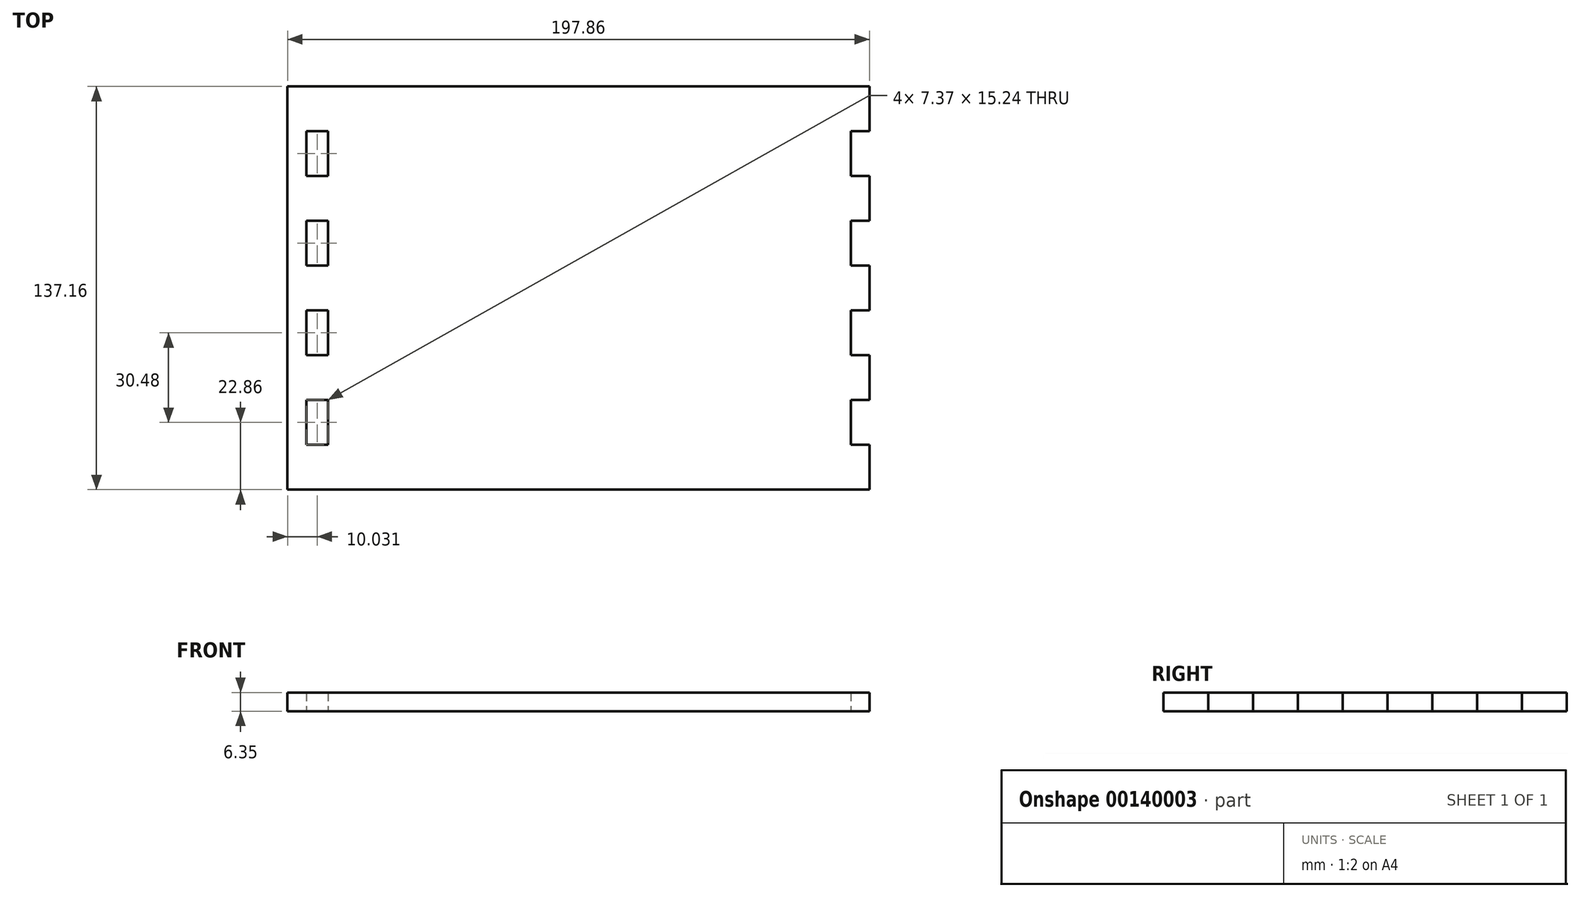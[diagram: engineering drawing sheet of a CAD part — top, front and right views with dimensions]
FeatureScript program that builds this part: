
annotation { "Feature Type Name" : "Feature", "Feature Type Description" : "" }
export const myFeature = defineFeature(function(context is Context, id is Id, definition is map)
    precondition{}
    {
        {
            var Q0;
            Q0=qCreatedBy(makeId("Top.planeOp"),FACE);
            var sketch = newSketch(context, id + "F0", { "sketchPlane" : qUnion([Q0])});
            skLineSegment(sketch, "E0.bottom", {"start": v(-69.3, 76.2) * mm, "end": v(108.5, 76.2) * mm});
            skLineSegment(sketch, "E0.top", {"start": v(-69.3, -60.96) * mm, "end": v(108.46, -60.96) * mm});
            skLineSegment(sketch, "E1", {"start": v(-76.67, 60.96) * mm, "end": v(-69.3, 60.96) * mm});
            skLineSegment(sketch, "E2", {"start": v(-69.3, 60.96) * mm, "end": v(-69.3, 45.72) * mm});
            skLineSegment(sketch, "E3", {"start": v(-69.3, 45.72) * mm, "end": v(-76.67, 45.72) * mm});
            skLineSegment(sketch, "E4", {"start": v(-76.67, 30.48) * mm, "end": v(-69.3, 30.48) * mm});
            skLineSegment(sketch, "E5", {"start": v(-69.3, 30.48) * mm, "end": v(-69.3, 15.24) * mm});
            skLineSegment(sketch, "E6", {"start": v(-69.3, 15.24) * mm, "end": v(-76.67, 15.24) * mm});
            skLineSegment(sketch, "E7", {"start": v(-76.67, 0) * mm, "end": v(-69.3, 0) * mm});
            skLineSegment(sketch, "E8", {"start": v(-69.3, 0) * mm, "end": v(-69.3, -15.24) * mm});
            skLineSegment(sketch, "E9", {"start": v(-69.3, -15.24) * mm, "end": v(-76.67, -15.24) * mm});
            skLineSegment(sketch, "E10", {"start": v(-76.67, -30.48) * mm, "end": v(-69.3, -30.48) * mm});
            skLineSegment(sketch, "E11", {"start": v(-69.3, -30.48) * mm, "end": v(-69.3, -45.72) * mm});
            skLineSegment(sketch, "E12", {"start": v(-69.3, -45.72) * mm, "end": v(-76.67, -45.72) * mm});
            skLineSegment(sketch, "E13", {"start": v(108.5, 76.2) * mm, "end": v(114.84, 76.2) * mm});
            skLineSegment(sketch, "E14", {"start": v(114.84, 76.2) * mm, "end": v(114.84, 60.96) * mm});
            skLineSegment(sketch, "E15", {"start": v(114.84, 60.96) * mm, "end": v(108.5, 60.96) * mm});
            skLineSegment(sketch, "E16", {"start": v(108.5, 60.96) * mm, "end": v(108.5, 45.72) * mm});
            skLineSegment(sketch, "E17", {"start": v(108.5, 45.72) * mm, "end": v(114.84, 45.72) * mm});
            skLineSegment(sketch, "E18", {"start": v(114.84, 45.72) * mm, "end": v(114.84, 30.48) * mm});
            skLineSegment(sketch, "E19", {"start": v(114.84, 30.48) * mm, "end": v(108.5, 30.48) * mm});
            skLineSegment(sketch, "E20", {"start": v(108.5, 30.48) * mm, "end": v(108.5, 15.24) * mm});
            skLineSegment(sketch, "E21", {"start": v(108.5, 15.24) * mm, "end": v(114.84, 15.24) * mm});
            skLineSegment(sketch, "E22", {"start": v(114.84, 15.24) * mm, "end": v(114.84, 0) * mm});
            skLineSegment(sketch, "E23", {"start": v(114.84, 0) * mm, "end": v(108.5, 0) * mm});
            skLineSegment(sketch, "E24", {"start": v(108.5, 0) * mm, "end": v(108.5, -15.24) * mm});
            skLineSegment(sketch, "E25", {"start": v(108.5, -15.24) * mm, "end": v(114.84, -15.24) * mm});
            skLineSegment(sketch, "E26", {"start": v(114.84, -15.24) * mm, "end": v(114.84, -30.48) * mm});
            skLineSegment(sketch, "E27", {"start": v(114.84, -30.48) * mm, "end": v(108.5, -30.48) * mm});
            skLineSegment(sketch, "E28", {"start": v(108.5, -30.48) * mm, "end": v(108.5, -45.72) * mm});
            skLineSegment(sketch, "E29", {"start": v(108.5, -45.72) * mm, "end": v(114.84, -45.72) * mm});
            skLineSegment(sketch, "E30", {"start": v(114.84, -60.96) * mm, "end": v(108.46, -60.96) * mm});
            skLineSegment(sketch, "E31", {"start": v(-69.3, 76.2) * mm, "end": v(-76.67, 76.2) * mm});
            skLineSegment(sketch, "E32", {"start": v(-76.67, -60.96) * mm, "end": v(-69.3, -60.96) * mm});
            skLineSegment(sketch, "E33", {"start": v(114.84, -45.72) * mm, "end": v(114.84, -60.96) * mm});
            skLineSegment(sketch, "E34", {"start": v(-76.67, -60.96) * mm, "end": v(-83.02, -60.96) * mm});
            skLineSegment(sketch, "E35", {"start": v(-83.02, -60.96) * mm, "end": v(-83.02, 76.2) * mm});
            skLineSegment(sketch, "E36", {"start": v(-83.02, 76.2) * mm, "end": v(-76.67, 76.2) * mm});
            skLineSegment(sketch, "E37", {"start": v(-76.67, 60.96) * mm, "end": v(-76.67, 45.72) * mm});
            skLineSegment(sketch, "E38", {"start": v(-76.67, 30.48) * mm, "end": v(-76.67, 15.24) * mm});
            skLineSegment(sketch, "E39", {"start": v(-76.67, 0) * mm, "end": v(-76.67, -15.24) * mm});
            skLineSegment(sketch, "E40", {"start": v(-76.67, -30.48) * mm, "end": v(-76.67, -45.72) * mm});
            skSolve(sketch);
        }
        {
            var Q0;
            Q0=makeQuery(id+"F0.imprint","IMPRINT",FACE,{"disambiguationData":[TD([[makeQuery(id+"F0.imprint","IMPRINT",EDGE,{"derivedFrom":sQuery(id+"F0.wireOp",EDGE,"E0.bottom")}),-1.0]])]});
            extrude(context, id + "F1", {"entities" : qUnion([Q0]), "depth" : 6.35 * mm});
        }
    });
